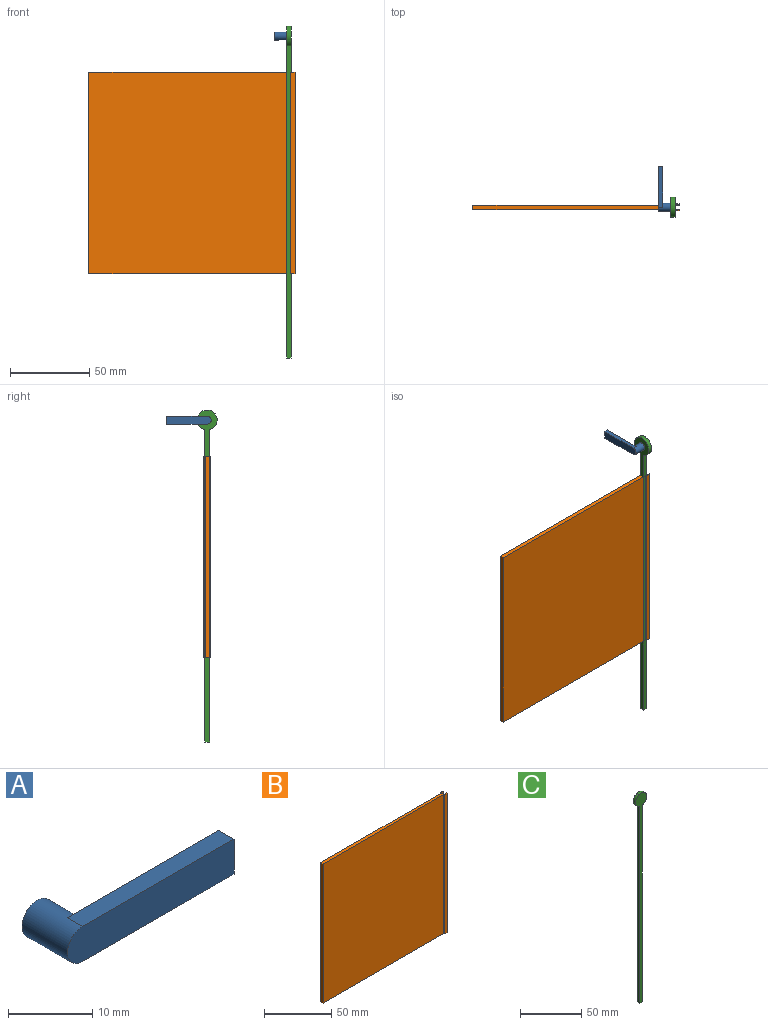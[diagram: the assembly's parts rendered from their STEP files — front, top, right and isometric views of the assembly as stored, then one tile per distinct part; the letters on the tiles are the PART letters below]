
ASSEMBLY  parts=3 mates=2
PART A: 7 faces, bbox 27.9x7.6x5.1 mm
  f0: cylinder r=2.54mm len=7.62mm, axis (0,1,0), area 101.3mm2, adj f1,f2,f4,f5,f6
  f1: plane 27.94x5.08mm, normal (0,-1,0), area 139.2mm2, adj f0,f3,f4,f5
  f2: plane 25.4x5.08mm, normal (0,1,0), area 118.9mm2, adj f0,f3,f4,f5
  f3: plane 5.08x2.54mm, normal (1,0,0), area 12.9mm2, adj f1,f2,f4,f5
  f4: plane 25.4x2.54mm, normal (0,0,-1), area 64.5mm2, adj f0,f1,f2,f3
  f5: plane 25.4x2.54mm, normal (0,0,1), area 64.5mm2, adj f0,f1,f2,f3
  f6: plane 5.08x5.08mm, normal (0,1,0), area 20.3mm2, adj f0
PART B: 14 faces, bbox 130x4.1x127 mm
  f0: plane 127x3.05mm, normal (1,0,0), area 387.1mm2, adj f2,f3,f10,f12
  f1: plane 127x2.54mm, normal (-1,0,0), area 322.6mm2, adj f2,f3,f4,f5
  f2: plane 130.05x4.06mm, normal (0,0,-1), area 327.2mm2, adj f0,f1,f4,f5,f6,f7,f8,f9
  f3: plane 130.05x4.06mm, normal (0,0,1), area 327.2mm2, adj f0,f1,f4,f5,f6,f7,f8,f9
  f4: plane 127x127mm, normal (0,-1,0), area 16129mm2, adj f1,f2,f3,f9
  f5: plane 127x127mm, normal (0,1,0), area 16129mm2, adj f1,f2,f3,f6
  f6: plane 127x0.76mm, normal (-1,0,0), area 96.8mm2, adj f2,f3,f5,f8
  f7: plane 127x3.05mm, normal (0,-1,0), area 387.1mm2, adj f2,f3,f9,f11
  f8: plane 127x3.05mm, normal (0,1,0), area 387.1mm2, adj f2,f3,f6,f13
  f9: plane 127x0.76mm, normal (-1,0,0), area 96.8mm2, adj f2,f3,f4,f7
  f10: plane 127x2.54mm, normal (0,1,0), area 322.6mm2, adj f0,f2,f3,f11
  f11: plane 127x0.51mm, normal (1,0,0), area 64.5mm2, adj f2,f3,f7,f10
  f12: plane 127x2.54mm, normal (0,-1,0), area 322.6mm2, adj f0,f2,f3,f13
  f13: plane 127x0.51mm, normal (1,0,0), area 64.5mm2, adj f2,f3,f8,f12
PART C: 8 faces, bbox 12.7x2.5x209.6 mm
  f0: plane 197.04x2.54mm, normal (-1,0,0), area 500.5mm2, adj f1,f3,f4,f5
  f1: plane 3.05x2.54mm, normal (0,0,-1), area 7.7mm2, adj f0,f2,f3,f4
  f2: plane 197.04x2.54mm, normal (1,0,0), area 500.5mm2, adj f1,f3,f4,f5
  f3: plane 209.55x12.7mm, normal (0,-1,0), area 726.9mm2, adj f0,f1,f2,f5
  f4: plane 209.55x12.7mm, normal (0,1,0), area 706.6mm2, adj f0,f1,f2,f5,f6
  f5: cylinder r=6.35mm len=12.7mm, axis (0,-1,0), area 93.5mm2, adj f0,f2,f3,f4
  f6: cylinder r=2.54mm len=5.08mm, axis (0,1,0), area 16.2mm2, adj f4,f7
  f7: plane 5.08x5.08mm, normal (0,1,0), area 20.3mm2, adj f6
PLACE A rot(axis=(0.71,0.71,0),180deg) t=(45.85,-5.5,91.32)mm
PLACE B t=(0.22,-4.23,1.35)mm
PLACE C rot(axis=(0,0,1),90deg) t=(50.93,8.1,-108.08)mm
MATE fastened C.f3 <-> B.f0  axis (1,0,0) through (53.47,-5.5,4.83)mm
MATE slider A.f0 <-> C.f5  axis (1,0,0) through (50.93,-5.5,91.32)mm
